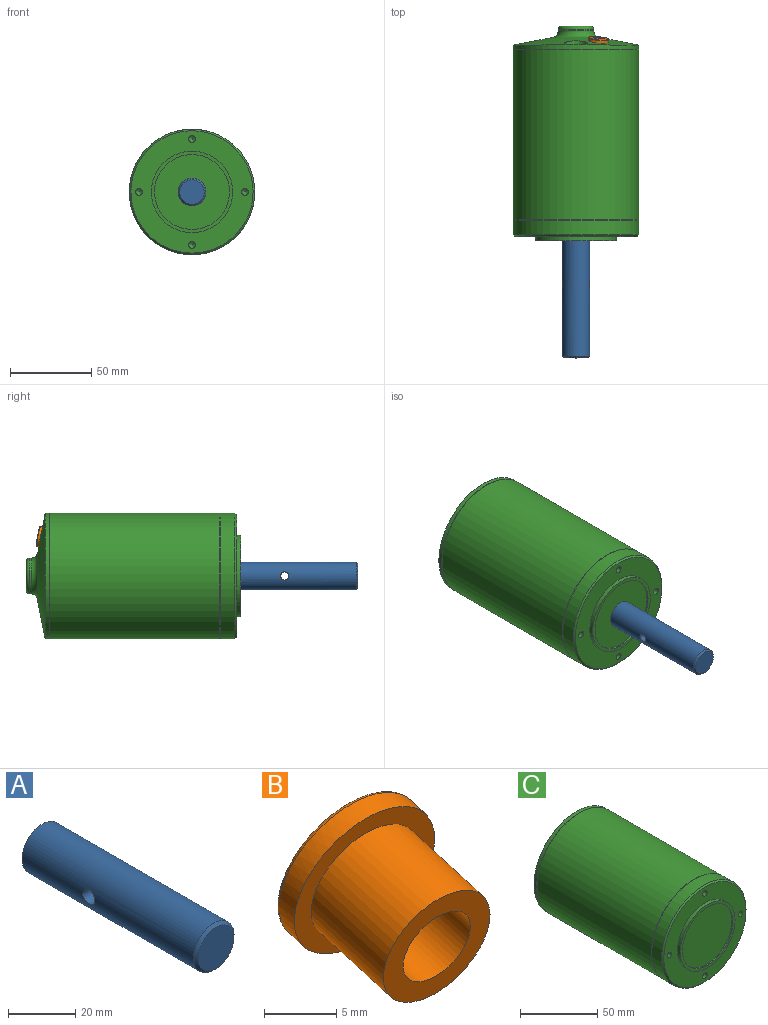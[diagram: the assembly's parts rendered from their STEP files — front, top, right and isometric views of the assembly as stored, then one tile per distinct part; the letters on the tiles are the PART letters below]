
ASSEMBLY  parts=3 mates=4
PART A: 5 faces, bbox 17x73x17 mm
  f0: cylinder r=8.5mm len=72mm, axis (0,-1,0), area 3805.6mm2, adj f2,f3,f4
  f1: plane 15x15mm, normal (0,-1,0), area 176.7mm2, adj f3
  f2: plane 17x17mm, normal (0,1,0), area 227mm2, adj f0
  f3: cone r=7.5mm half-angle=45deg, axis (0,1,0), area 71.1mm2, adj f0,f1
  f4: cylinder r=2.5mm len=17mm, axis (1,0,0), area 261.2mm2, adj f0
PART B: 8 faces, bbox 13.5x11.9x13.3 mm
  f0: plane 11.85x11.74mm, normal (0.1,0.98,0.17), area 77mm2, adj f6,f7
  f1: cylinder r=6.25mm len=12.61mm, axis (-0.1,-0.98,-0.17), area 66.8mm2, adj f2,f6
  f2: plane 12.44x12.33mm, normal (-0.1,-0.98,-0.17), area 51.8mm2, adj f1,f3
  f3: cylinder r=4.75mm len=10.69mm, axis (-0.1,-0.98,-0.17), area 238.8mm2, adj f2,f4
  f4: plane 9.46x9.37mm, normal (-0.1,-0.98,-0.17), area 42.6mm2, adj f3,f5
  f5: cylinder r=3mm len=10.67mm, axis (-0.1,-0.98,-0.17), area 182.8mm2, adj f4,f7
  f6: torus R=5.95mm, axis (0.1,0.98,0.17), area 18.2mm2, adj f0,f1
  f7: torus R=3.3mm, axis (0.1,0.98,0.17), area 9.2mm2, adj f0,f5
PART C: 30 faces, bbox 77x131.7x77 mm
  f0: cone r=0mm half-angle=59deg, axis (0,-1,0), area 16.2mm2, adj f1
  f1: cylinder r=2.1mm len=15.8mm, axis (0,-1,0), area 208.5mm2, adj f0,f16
  f2: cone r=0mm half-angle=59deg, axis (0,-1,0), area 16.2mm2, adj f3
  f3: cylinder r=2.1mm len=15.8mm, axis (0,-1,0), area 208.5mm2, adj f2,f16
  f4: cone r=0mm half-angle=59deg, axis (0,-1,0), area 16.2mm2, adj f5
  f5: cylinder r=2.1mm len=15.8mm, axis (0,-1,0), area 208.5mm2, adj f4,f16
  f6: torus R=15mm, axis (0,-1,0), area 421.1mm2, adj f7,f23
  f7: cone r=38.5mm half-angle=79deg, axis (0,-1,0), area 3871.1mm2, adj f6,f8,f26,f29
  f8: cylinder r=38.5mm len=77mm, axis (0,-1,0), area 604.8mm2, adj f7,f9,f27
  f9: plane 77x77mm, normal (0,-1,0), area 60.3mm2, adj f8,f10
  f10: cone r=38.5mm half-angle=45deg, axis (0,-1,0), area 85.2mm2, adj f9,f11
  f11: cylinder r=38.5mm len=104.5mm, axis (0,-1,0), area 25278.8mm2, adj f10,f12
  f12: cone r=38.5mm half-angle=45deg, axis (0,1,0), area 85.2mm2, adj f11,f13
  f13: plane 77x77mm, normal (0,1,0), area 60.3mm2, adj f12,f14
  f14: cylinder r=38.5mm len=77mm, axis (0,-1,0), area 2177.1mm2, adj f13,f15
  f15: cone r=37.5mm half-angle=45deg, axis (0,1,0), area 337.7mm2, adj f14,f16
  f16: plane 75x75mm, normal (0,-1,0), area 2399mm2, adj f1,f3,f5,f15,f17,f25
  f17: cylinder r=25mm len=50mm, axis (0,-1,0), area 392.7mm2, adj f16,f18
  f18: plane 50x50mm, normal (0,-1,0), area 301.6mm2, adj f17,f19
  f19: cylinder r=23mm len=46mm, axis (0,-1,0), area 144.5mm2, adj f18,f20
  f20: plane 46x46mm, normal (0,-1,0), area 1661.9mm2, adj f19
  f21: plane 18x18mm, normal (0,1,0), area 254.5mm2, adj f22
  f22: torus R=9mm, axis (0,-1,0), area 202.8mm2, adj f21,f23
  f23: cylinder r=11mm len=22mm, axis (0,-1,0), area 73.1mm2, adj f6,f22
  f24: cone r=0mm half-angle=59deg, axis (0,-1,0), area 16.2mm2, adj f25
  f25: cylinder r=2.1mm len=15.8mm, axis (0,-1,0), area 208.5mm2, adj f16,f24
  f26: cylinder r=7mm len=14mm, axis (0,-1,0), area 50.9mm2, adj f7,f27
  f27: plane 14x13.25mm, normal (0,1,0), area 150.4mm2, adj f8,f26
  f28: plane 9.46x9.37mm, normal (0.1,0.98,0.17), area 70.9mm2, adj f29
  f29: cylinder r=4.75mm len=10.69mm, axis (0.1,0.98,0.17), area 237.6mm2, adj f7,f28
PLACE A at identity
PLACE B at identity
PLACE C at identity fixed
MATE planar A.f0 <-> C.f6  axis (0,1,0) through (0,-1.5,0)mm
MATE cylindrical C.f29 <-> B.f6  axis (0.1,0.98,0.17) through (13.37,115.74,23.16)mm
MATE cylindrical A.f0 <-> C.f6  axis (0,-1,0) through (0,-1.5,0)mm
MATE planar C.f29 <-> B.f6  axis (0.1,0.98,0.17) through (12.99,111.79,22.49)mm
